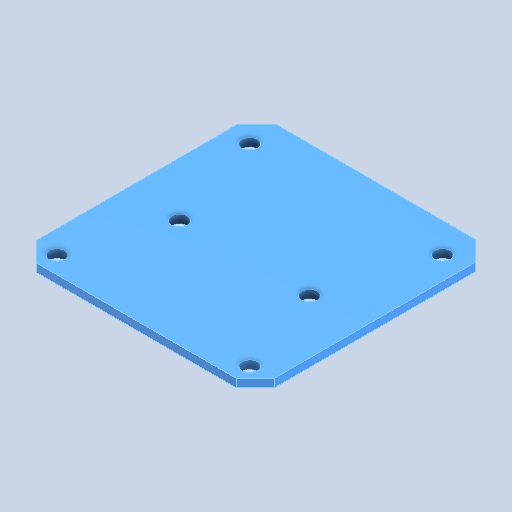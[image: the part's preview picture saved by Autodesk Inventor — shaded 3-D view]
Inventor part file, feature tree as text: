
AUTODESK INVENTOR PART (.ipt)
format: ipt  version: 2023.1 (Build 271208000, 208)  size: 97,792 bytes
history: native  units: in
note: dims shown in document units (in); Inventor stores cm internally (conversion verified against a paired STEP export)
features: chamfer x1
ambient origin geometry x8: Origin, YZ Plane, XZ Plane, XY Plane, X Axis, Y Axis, Z Axis, Center Point
bodies: Solid1 (feature_tree)
feature tree (1):
  chamfer  "Chamfer1"  [1 undecoded]
note: 1 required parameter value undecoded (feature->parameter linkage not recoverable at this tier; creation-order binding heuristic only, values carry confidence <= 0.55)
